# Revit family: Indirect-Water-Heater_AO_Smith-IT-750_B_B
name_source: partatom
category: Mechanical Equipment
revit_build: Autodesk Revit 2016 (Build: 20170117_1200(x64)
units: mm (PartAtom-declared; Revit-internal decimal feet)

## family parameters
Always vertical = Yes
Cut with Voids When Loaded = No
OmniClass Number = 23.75.00.00
OmniClass Title = Climate Control (HVAC)
Part Type = Normal
Room Calculation Point = No
Round Connector Dimension = Use Radius
Shared = No
Work Plane-Based = No

## types (1)
- IT 750 B B
    1e Maintenance (check-up) = 3 maanden na installatie
    2nd Maintenance (general maintenance) = 12 maanden na installatie
    Assembly Code = D3010
    BIM Content Developer = CAD & Company
    BIM Content Developer URL = http://www.cadcompany.be
    Category = Mechanical Equipment
    Cold Water Connection R = 1 1/2"
    Description = Indirecte Boiler met 1 warmtewisselaar
    Destination / Counrty = België
    Diameter (with insulation) = 930 mm  [stored 3.05118 ft]
    Diameter (without insulation) = 750 mm  [stored 2.46063 ft]
    Draw-off Capacity @ ΔT = 28°C after 120 min. = 8158.0 L
    Draw-off Capacity @ ΔT = 28°C after 30 min. = 2998.0 L
    Draw-off Capacity @ ΔT = 28°C after 60 min. = 4718.0 L
    Draw-off Capacity @ ΔT = 28°C after 90 min. = 6438.0 L
    Draw-off Capacity @ ΔT = 44°C after 120 min. = 5192.0 L
    Draw-off Capacity @ ΔT = 44°C after 30 min. = 1908.0 L
    Draw-off Capacity @ ΔT = 44°C after 60 min. = 3002.0 L
    Draw-off Capacity @ ΔT = 44°C after 90 min. = 4097.0 L
    Draw-off Capacity @ ΔT = 50°C after 120 min. = 4569.0 L
    Draw-off Capacity @ ΔT = 50°C after 30 min. = 1679.0 L
    Draw-off Capacity @ ΔT = 50°C after 60 min. = 2642.0 L
    Draw-off Capacity @ ΔT = 50°C after 90 min. = 3605.0 L
    Draw-off Capacity @ ΔT = 55°C after 120 min. = 4153.0 L
    Draw-off Capacity @ ΔT = 55°C after 30 min. = 1526.0 L
    Draw-off Capacity @ ΔT = 55°C after 60 min. = 2402.0 L
    Draw-off Capacity @ ΔT = 55°C after 90 min. = 3278.0 L
    Draw-off Capacity @ ΔT = 70°C after 120 min. = 3263.0 L
    Draw-off Capacity @ ΔT = 70°C after 30 min. = 1199.0 L
    Draw-off Capacity @ ΔT = 70°C after 60 min. = 1887.0 L
    Draw-off Capacity @ ΔT = 70°C after 90 min. = 2575.0 L
    Empty Weight = 254.00 kg
    Flow Rate - Volume L/h = 4816
    Heating Up Time @ ΔT = 28°C = 13
    Heating Up Time @ ΔT = 44°C = 20
    Heating Up Time @ ΔT = 50°C = 23
    Heating Up Time @ ΔT = 55°C = 25
    Heating Up Time @ ΔT = 70°C = 32
    Height (with insulation) = 2035 mm  [stored 6.67651 ft]
    Height (without insulation) = 2000 mm  [stored 6.56168 ft]
    Height Cold Water Inlet = 85 mm  [stored 0.278871 ft]
    Height Warm Water Outlet = 2000 mm  [stored 6.56168 ft]
    Host = Unhosted
    Hot / Warm Water Connection R = 1 1/2"
    Insulation Thickness = 90 mm  [stored 0.295276 ft]
    Maintenance Interval = 12 maanden
    Manufacturer = A.O. Smith Water Products Company b.v.
    Manufacturer Number = E 7110
E 7110
E 7110
    Max. Operating Pressure - bottom heat exchanger = 1600000.0 Pa
    Max. Operating Pressure - tank = 1000000.0 Pa
    Max. Tempature - bottom heat exchanger = 110 °C
    Max. Temperature - tank = 95 °C
    Model = IT 750 B B
    NLSfB = 51.11
    Nominal Output - bottom heat exchanger = 112000 W
    Operating Weight = 979.00 kg
    Packaging Height = 2150 mm
    Packaging Length = 870 mm  [stored 2.85433 ft]
    Packaging Width = 870 mm  [stored 2.85433 ft]
    Pressure Loss - bottom heat exchanger 80ºC/60ºC = 12800.0 Pa
    Product Documentation Link = https://www.aosmithinternational.com
    Product Instruction Link = https://www.aosmithinternational.com
    Productcode = 8717449180294
    Productversion = 1.0
    Recovery Rate @ ΔT = 28°C (ltr/hr) = 3440
    Recovery Rate @ ΔT = 44°C (ltr/hr) = 2189
    Recovery Rate @ ΔT = 50°C (ltr/hr) = 1926
    Recovery Rate @ ΔT = 55°C (ltr/hr) = 1751
    Recovery Rate @ ΔT = 70°C (ltr/hr) = 1376
    Serial Number = 8717449180294
    Stand-by Loss = 0 W
    Stand-by Loss - daily (Watt/24H) = 0
    Storage Capacity - bottom heat exchanger = 31.6 m³
    Storage Capacity - tank = 725 m³
    Surface bottom heat Exchanger = 3.72 m²
    T&P Connection Rp = 1"
    Transport Weight = 260.00 kg
    Type of Packaging = Plastic en Hout
    URL = www.aosmith.be
    Warranty on Parts = 12 maanden
    Warranty on Tank = 36 maanden
    Workspace Diameter = 1930 mm  [stored 6.33202 ft]
    Workspace Height = 3035 mm  [stored 9.95735 ft]

note: [stored X ft] marks values corroborated as IEEE doubles in the binary element streams (Revit-internal decimal feet)

## geometry (parser evidence)
native form markers: Blend x2, Sweep x21
no freeform markers — native parametric forms only
